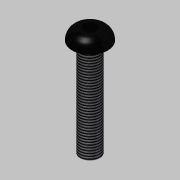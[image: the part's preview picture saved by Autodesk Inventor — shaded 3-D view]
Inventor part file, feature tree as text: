
AUTODESK INVENTOR PART (.ipt)
format: ipt  version: 2014 (Build 180170000, 170)  size: 113,664 bytes
history: native  units: mm
features: extrude x3, sketch x3, fillet x1, thread x1, reference x1
ambient origin geometry x8: Origin, YZ Plane, XZ Plane, XY Plane, X Axis, Y Axis, Z Axis, Center Point
bodies: Solid1 (feature_tree)
feature tree (9):
  extrude  "Extrusion1"  Depth=20.0mm TaperAngle=0.0deg
  extrude  "Extrusion2"  Depth=2.3mm TaperAngle=0.0deg
  fillet  "Fillet1"  Radius=2.2mm
  extrude  "Extrusion4"  Depth=10.0mm TaperAngle=0.0deg
  thread  "Thread1"  [1 undecoded]
  sketch  "Sketch1"  dims[d0=4.0mm d1=20.0mm d2=0.0mm]
  reference  "Reference1"
  sketch  "Sketch2"  dims[d3=7.3mm d4=2.3mm d5=0.0mm d6=2.2mm]
  sketch  "Sketch4"  dims[d10=2.5mm d11=4.0mm d12=0.0mm d13=10.0mm d14=0.0mm]
note: 1 required parameter value undecoded (feature->parameter linkage not recoverable at this tier; creation-order binding heuristic only, values carry confidence <= 0.55)
